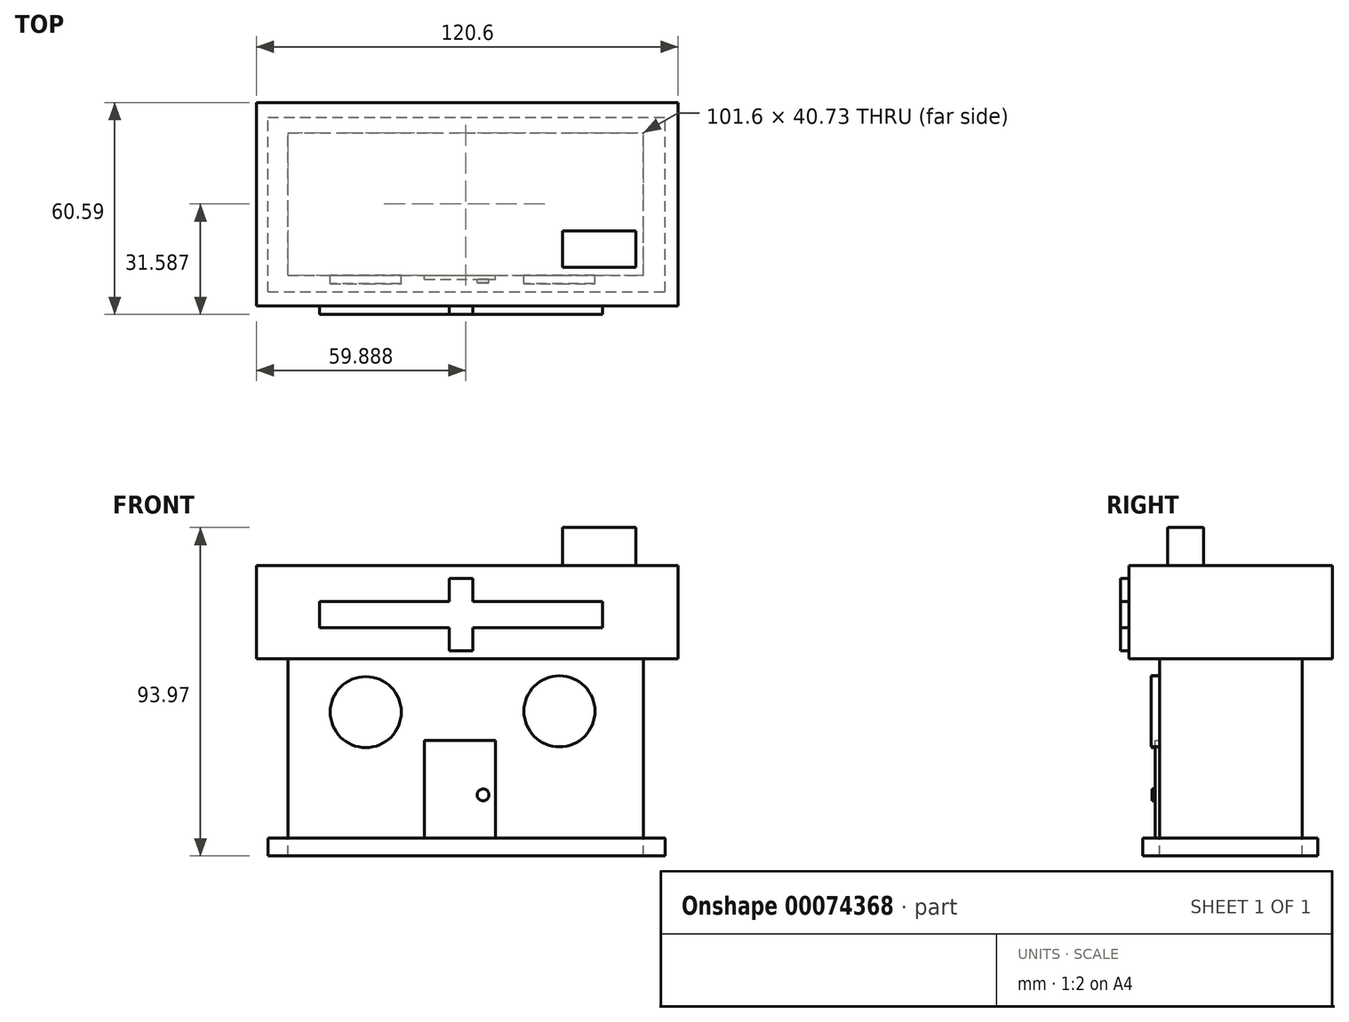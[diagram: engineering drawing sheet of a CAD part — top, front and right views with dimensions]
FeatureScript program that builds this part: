
annotation { "Feature Type Name" : "Feature", "Feature Type Description" : "" }
export const myFeature = defineFeature(function(context is Context, id is Id, definition is map)
    precondition{}
    {
        {
            var Q0;
            Q0=qCreatedBy(makeId("Front.planeOp"),FACE);
            var sketch = newSketch(context, id + "F0", { "sketchPlane" : qUnion([Q0])});
            skLineSegment(sketch, "E0.bottom", {"start": v(-49.4, 17.29) * mm, "end": v(52.2, 17.29) * mm});
            skLineSegment(sketch, "E0.top", {"start": v(-49.4, -51.3) * mm, "end": v(52.2, -51.3) * mm});
            skLineSegment(sketch, "E0.left", {"start": v(-49.4, 17.29) * mm, "end": v(-49.4, -51.3) * mm});
            skLineSegment(sketch, "E0.right", {"start": v(52.2, 17.29) * mm, "end": v(52.2, -51.3) * mm});
            skSolve(sketch);
        }
        {
            var Q0;
            Q0=makeQuery(id+"F0.imprint","IMPRINT",FACE,{"disambiguationData":[TD([[makeQuery(id+"F0.imprint","IMPRINT",EDGE,{"derivedFrom":sQuery(id+"F0.wireOp",EDGE,"E0.bottom")}),-1.0]])]});
            extrude(context, id + "F1", {"entities" : qUnion([Q0]), "depth" : 40.73 * mm});
        }
        {
            var Q0;
            Q0=makeQuery(id+"F1.opExtrude","SWEPT_FACE",FACE,{"disambiguationData":[OSD([sQuery(id+"F0.wireOp",EDGE,"E0.top")])]});
            var sketch = newSketch(context, id + "F2", { "sketchPlane" : qUnion([Q0])});
            skLineSegment(sketch, "E1.bottom", {"start": v(-55.2, 45.52) * mm, "end": v(58.37, 45.52) * mm});
            skLineSegment(sketch, "E1.top", {"start": v(-55.2, -4.46) * mm, "end": v(58.37, -4.46) * mm});
            skLineSegment(sketch, "E1.left", {"start": v(-55.2, 45.52) * mm, "end": v(-55.2, -4.46) * mm});
            skLineSegment(sketch, "E1.right", {"start": v(58.37, 45.52) * mm, "end": v(58.37, -4.46) * mm});
            skSolve(sketch);
        }
        {
            var Q0;
            Q0=makeQuery(id+"F2.imprint","IMPRINT",FACE,{"disambiguationData":[TD([[makeQuery(id+"F2.imprint","IMPRINT",EDGE,{"derivedFrom":sQuery(id+"F2.wireOp",EDGE,"E1.bottom")}),-1.0]])]});
            extrude(context, id + "F3", {"entities" : qUnion([Q0]), "depth" : 5.08 * mm});
        }
        {
            var Q0;
            Q0=qCreatedBy(makeId("Top.planeOp"),FACE);
            var sketch = newSketch(context, id + "F4", { "sketchPlane" : qUnion([Q0])});
            skLineSegment(sketch, "E2.bottom", {"start": v(-58.48, 8.64) * mm, "end": v(62.12, 8.64) * mm});
            skLineSegment(sketch, "E2.top", {"start": v(-58.48, -49.55) * mm, "end": v(62.12, -49.55) * mm});
            skLineSegment(sketch, "E2.left", {"start": v(-58.48, 8.64) * mm, "end": v(-58.48, -49.55) * mm});
            skLineSegment(sketch, "E2.right", {"start": v(62.12, 8.64) * mm, "end": v(62.12, -49.55) * mm});
            skSolve(sketch);
        }
        {
            var Q0;
            Q0=makeQuery(id+"F4.imprint","IMPRINT",FACE,{"disambiguationData":[TD([[makeQuery(id+"F4.imprint","IMPRINT",EDGE,{"derivedFrom":sQuery(id+"F4.wireOp",EDGE,"E2.bottom")}),-1.0]])]});
            extrude(context, id + "F5", {"entities" : qUnion([Q0]), "operationType" : NewBodyOperationType.ADD, "depth" : 26.67 * mm});
        }
        {
            var Q0;
            Q0=qCreatedBy(makeId("Top.planeOp"),FACE);
            var sketch = newSketch(context, id + "F6", { "sketchPlane" : qUnion([Q0])});
            skLineSegment(sketch, "E3.bottom", {"start": v(29.1, -28.12) * mm, "end": v(49.98, -28.12) * mm});
            skLineSegment(sketch, "E3.top", {"start": v(29.1, -38.44) * mm, "end": v(49.98, -38.44) * mm});
            skLineSegment(sketch, "E3.left", {"start": v(29.1, -28.12) * mm, "end": v(29.1, -38.44) * mm});
            skLineSegment(sketch, "E3.right", {"start": v(49.98, -28.12) * mm, "end": v(49.98, -38.44) * mm});
            skSolve(sketch);
        }
        {
            var Q0;
            Q0 = qSketchRegion(id + "F6", true);
            extrude(context, id + "F7", {"entities" : qUnion([Q0]), "operationType" : NewBodyOperationType.ADD, "depth" : 37.6 * mm});
        }
        {
            var Q0;
            Q0=makeQuery(id+"F1.opExtrude","CAP_FACE",FACE,{"disambiguationData":[OSD([sQuery(id+"F0.wireOp",EDGE,"E0.bottom"),sQuery(id+"F0.wireOp",EDGE,"E0.top"),sQuery(id+"F0.wireOp",EDGE,"E0.left"),sQuery(id+"F0.wireOp",EDGE,"E0.right")])],"isStart":false});
            var sketch = newSketch(context, id + "F8", { "sketchPlane" : qUnion([Q0])});
            skCircle(sketch, "E4", {"center": v(-27.22, -15.21) * mm, "radius": 10.16 * mm});
            skCircle(sketch, "E5", {"center": v(28.16, -14.98) * mm, "radius": 10.16 * mm});
            skSolve(sketch);
        }
        {
            var Q0;
            Q0 = qSketchRegion(id + "F8", true);
            extrude(context, id + "F9", {"entities" : qUnion([Q0]), "operationType" : NewBodyOperationType.ADD, "depth" : 2.4 * mm});
        }
        {
            var Q0;
            Q0=makeQuery(id+"F1.opExtrude","CAP_FACE",FACE,{"disambiguationData":[OSD([sQuery(id+"F0.wireOp",EDGE,"E0.bottom"),sQuery(id+"F0.wireOp",EDGE,"E0.top"),sQuery(id+"F0.wireOp",EDGE,"E0.left"),sQuery(id+"F0.wireOp",EDGE,"E0.right")])],"isStart":false});
            var sketch = newSketch(context, id + "F10", { "sketchPlane" : qUnion([Q0])});
            skLineSegment(sketch, "E6.bottom", {"start": v(-10.44, -51.3) * mm, "end": v(9.88, -51.3) * mm});
            skLineSegment(sketch, "E6.top", {"start": v(-10.44, -23.35) * mm, "end": v(9.88, -23.35) * mm});
            skLineSegment(sketch, "E6.left", {"start": v(-10.44, -51.3) * mm, "end": v(-10.44, -23.35) * mm});
            skLineSegment(sketch, "E6.right", {"start": v(9.88, -51.3) * mm, "end": v(9.88, -23.35) * mm});
            skSolve(sketch);
        }
        {
            var Q0;
            Q0 = qSketchRegion(id + "F10", true);
            extrude(context, id + "F11", {"entities" : qUnion([Q0]), "depth" : 1.23 * mm});
        }
        {
            var Q0;
            Q0=makeQuery(id+"F11.opExtrude","CAP_FACE",FACE,{"disambiguationData":[OSD([sQuery(id+"F10.wireOp",EDGE,"E6.bottom"),sQuery(id+"F10.wireOp",EDGE,"E6.top"),sQuery(id+"F10.wireOp",EDGE,"E6.left"),sQuery(id+"F10.wireOp",EDGE,"E6.right")])],"isStart":false});
            var sketch = newSketch(context, id + "F12", { "sketchPlane" : qUnion([Q0])});
            skCircle(sketch, "E7", {"center": v(6.34, -38.91) * mm, "radius": 1.7 * mm});
            skSolve(sketch);
        }
        {
            var Q0;
            Q0 = qSketchRegion(id + "F12", true);
            extrude(context, id + "F13", {"entities" : qUnion([Q0]), "operationType" : NewBodyOperationType.ADD, "depth" : 1 * mm});
        }
        {
            var Q0;
            Q0=makeQuery(id+"F5.opExtrude","SWEPT_FACE",FACE,{"disambiguationData":[OSD([sQuery(id+"F4.wireOp",EDGE,"E2.top")])]});
            var sketch = newSketch(context, id + "F14", { "sketchPlane" : qUnion([Q0])});
            skLineSegment(sketch, "E8.rect.bottom", {"start": v(-40.42, 16.46) * mm, "end": v(40.42, 16.46) * mm});
            skLineSegment(sketch, "E8.rect.top", {"start": v(-40.42, 8.95) * mm, "end": v(40.42, 8.95) * mm});
            skLineSegment(sketch, "E8.rect.left", {"start": v(-40.42, 16.46) * mm, "end": v(-40.42, 8.95) * mm});
            skLineSegment(sketch, "E8.rect.right", {"start": v(40.42, 16.46) * mm, "end": v(40.42, 8.95) * mm});
            skPoint(sketch, "E8.rect.middle", {"position": v(0, 12.7) * mm});
            skLineSegment(sketch, "E9.rect.bottom", {"start": v(-3.35, 23.03) * mm, "end": v(3.35, 23.03) * mm});
            skLineSegment(sketch, "E9.rect.top", {"start": v(-3.35, 2.38) * mm, "end": v(3.35, 2.38) * mm});
            skLineSegment(sketch, "E9.rect.left", {"start": v(-3.35, 23.03) * mm, "end": v(-3.35, 2.38) * mm});
            skLineSegment(sketch, "E9.rect.right", {"start": v(3.35, 23.03) * mm, "end": v(3.35, 2.38) * mm});
            skSolve(sketch);
        }
        {
            var Q0;
            Q0 = qSketchRegion(id + "F14", true);
            extrude(context, id + "F15", {"entities" : qUnion([Q0]), "operationType" : NewBodyOperationType.ADD, "depth" : 2.4 * mm});
        }
    });
